# Revit family: S90.196.xxx(.WDAS)_with 3 shelves_4+6 drawers
name_source: partatom
category: Möbelsysteme
revit_build: Autodesk Revit 2015 (Build: 20160512_1515(x64)
units: mm (PartAtom-declared; Revit-internal decimal feet)

## types (27) — shared parameters
Air duct distance = 130 mm  [stored 0.426509 ft]
Beschreibung = GS-tested safety storage cabinets for unrestricted storage of flammable hazardous materials in work areas in accordance with EN 14470-1 and TRGS 510 with a fire resistance of 90 (Type 90)
Cabinet depth = 617 mm
Cabinet height = 1968 mm  [stored 6.45669 ft]
Diff. pressure (Air change 10 times) = 5.0 Pa
Hersteller = asecos GmbH
Price information = Price from fall 2017
Price information 2 = Prices are ex works and without taxes and shipping
Product video = https://www.youtube.com
URL = https://www.asecos.com

## per-type parameters (varying)
- S90.196.060 with 3 shelves, warning yellow: 1200 mm 3 shelves=Nein; 1200 mm 4 drawers=Nein; 1200 mm 6 drawers=Nein; 600 mm 3 shelves=Ja; 600 mm 4 drawers=Nein; 600 mm 6 drawers=Nein; 900 mm 3 shelves=Nein; 900 mm 4 drawers=Nein; 900 mm 6 drawers=Nein; Air change 10 times=1.1 L/s; Bestellnummer DACH=30228-002-30249; Cabinet & door colour=RAL 1004 warning yellow; Cabinet width=597 mm; Distributed load=8.77 kN/m²; Door width=514 mm  [stored 1.68635 ft]; Double door=Nein; Handle position=514 mm  [stored 1.68635 ft]; Kosten=2093 $; Modell=S90.196.060.WDAS with 3 shelves and door open arrest system; Order No. Global=30228-002-33659; Single door=Ja; Sticker position lb=269 mm; Sticker position ls=555 mm; Sticker position rb=0 mm  [stored 0 ft]; Typenbild=30227-002.jpg; ex. air 2 depth=5 mm  [stored 0.0164042 ft]; ex. air pos. 1=368 mm  [stored 1.20735 ft]; ex.air 1 depth=-5 mm  [stored -0.0164042 ft]
- S90.196.060 with 3 shelves, light grey: 1200 mm 3 shelves=Nein; 1200 mm 4 drawers=Nein; 1200 mm 6 drawers=Nein; 600 mm 3 shelves=Ja; 600 mm 4 drawers=Nein; 600 mm 6 drawers=Nein; 900 mm 3 shelves=Nein; 900 mm 4 drawers=Nein; 900 mm 6 drawers=Nein; Air change 10 times=1.1 L/s; Bestellnummer DACH=30228-001-30249; Cabinet & door colour=RAL 7035 Light grey; Cabinet width=597 mm; Distributed load=8.77 kN/m²; Door width=514 mm  [stored 1.68635 ft]; Double door=Nein; Handle position=514 mm  [stored 1.68635 ft]; Kosten=2093 $; Modell=S90.196.060.WDAS with 3 shelves and door open arrest system; Order No. Global=30228-001-33659; Single door=Ja; Sticker position lb=269 mm; Sticker position ls=555 mm; Sticker position rb=0 mm  [stored 0 ft]; Typenbild=30227-001.jpg; ex. air 2 depth=5 mm  [stored 0.0164042 ft]; ex. air pos. 1=368 mm  [stored 1.20735 ft]; ex.air 1 depth=-5 mm  [stored -0.0164042 ft]
- S90.196.060 with 3 shelves, pure white: 1200 mm 3 shelves=Nein; 1200 mm 4 drawers=Nein; 1200 mm 6 drawers=Nein; 600 mm 3 shelves=Ja; 600 mm 4 drawers=Nein; 600 mm 6 drawers=Nein; 900 mm 3 shelves=Nein; 900 mm 4 drawers=Nein; 900 mm 6 drawers=Nein; Air change 10 times=1.1 L/s; Bestellnummer DACH=30228-005-30249; Cabinet & door colour=RAL 9010 Pure white; Cabinet width=597 mm; Distributed load=8.77 kN/m²; Door width=514 mm  [stored 1.68635 ft]; Double door=Nein; Handle position=514 mm  [stored 1.68635 ft]; Kosten=2093 $; Modell=S90.196.060.WDAS with 3 shelves and door open arrest system; Order No. Global=30228-005-33659; Single door=Ja; Sticker position lb=269 mm; Sticker position ls=555 mm; Sticker position rb=0 mm  [stored 0 ft]; Typenbild=30227-001.jpg; ex. air 2 depth=5 mm  [stored 0.0164042 ft]; ex. air pos. 1=368 mm  [stored 1.20735 ft]; ex.air 1 depth=-5 mm  [stored -0.0164042 ft]
- S90.196.060 with 4 drawers, warning yellow: 1200 mm 3 shelves=Nein; 1200 mm 4 drawers=Nein; 1200 mm 6 drawers=Nein; 600 mm 3 shelves=Nein; 600 mm 4 drawers=Ja; 600 mm 6 drawers=Nein; 900 mm 3 shelves=Nein; 900 mm 4 drawers=Nein; 900 mm 6 drawers=Nein; Air change 10 times=1.1 L/s; Bestellnummer DACH=30228-002-30267; Cabinet & door colour=RAL 1004 warning yellow; Cabinet width=597 mm; Distributed load=8.77 kN/m²; Door width=514 mm  [stored 1.68635 ft]; Double door=Nein; Handle position=514 mm  [stored 1.68635 ft]; Kosten=2373 $; Modell=S90.196.060.WDAS with 4 drawers and door open arrest system; Order No. Global=30228-002-33681; Single door=Ja; Sticker position lb=269 mm; Sticker position ls=555 mm; Sticker position rb=0 mm  [stored 0 ft]; Typenbild=30227-002.jpg; ex. air 2 depth=5 mm  [stored 0.0164042 ft]; ex. air pos. 1=368 mm  [stored 1.20735 ft]; ex.air 1 depth=-5 mm  [stored -0.0164042 ft]
- S90.196.060 with 4 drawers, light grey: 1200 mm 3 shelves=Nein; 1200 mm 4 drawers=Nein; 1200 mm 6 drawers=Nein; 600 mm 3 shelves=Nein; 600 mm 4 drawers=Ja; 600 mm 6 drawers=Nein; 900 mm 3 shelves=Nein; 900 mm 4 drawers=Nein; 900 mm 6 drawers=Nein; Air change 10 times=1.1 L/s; Bestellnummer DACH=30228-001-30267; Cabinet & door colour=RAL 7035 Light grey; Cabinet width=597 mm; Distributed load=8.77 kN/m²; Door width=514 mm  [stored 1.68635 ft]; Double door=Nein; Handle position=514 mm  [stored 1.68635 ft]; Kosten=2373 $; Modell=S90.196.060.WDAS with 4 drawer and door open arrest systems; Order No. Global=30228-001-33681; Single door=Ja; Sticker position lb=269 mm; Sticker position ls=555 mm; Sticker position rb=0 mm  [stored 0 ft]; Typenbild=30227-001.jpg; ex. air 2 depth=5 mm  [stored 0.0164042 ft]; ex. air pos. 1=368 mm  [stored 1.20735 ft]; ex.air 1 depth=-5 mm  [stored -0.0164042 ft]
- S90.196.060 with 4 drawers, pure white: 1200 mm 3 shelves=Nein; 1200 mm 4 drawers=Nein; 1200 mm 6 drawers=Nein; 600 mm 3 shelves=Nein; 600 mm 4 drawers=Ja; 600 mm 6 drawers=Nein; 900 mm 3 shelves=Nein; 900 mm 4 drawers=Nein; 900 mm 6 drawers=Nein; Air change 10 times=1.1 L/s; Bestellnummer DACH=30228-005-30267; Cabinet & door colour=RAL 9010 Pure white; Cabinet width=597 mm; Distributed load=8.77 kN/m²; Door width=514 mm  [stored 1.68635 ft]; Double door=Nein; Handle position=514 mm  [stored 1.68635 ft]; Kosten=2373 $; Modell=S90.196.060.WDAS with 4 drawers and door open arrest system; Order No. Global=30228-005-33681; Single door=Ja; Sticker position lb=269 mm; Sticker position ls=555 mm; Sticker position rb=0 mm  [stored 0 ft]; Typenbild=30227-001.jpg; ex. air 2 depth=5 mm  [stored 0.0164042 ft]; ex. air pos. 1=368 mm  [stored 1.20735 ft]; ex.air 1 depth=-5 mm  [stored -0.0164042 ft]
- S90.196.060 with 6 drawers, warning yellow: 1200 mm 3 shelves=Nein; 1200 mm 4 drawers=Nein; 1200 mm 6 drawers=Nein; 600 mm 3 shelves=Nein; 600 mm 4 drawers=Nein; 600 mm 6 drawers=Ja; 900 mm 3 shelves=Nein; 900 mm 4 drawers=Nein; 900 mm 6 drawers=Nein; Air change 10 times=1.1 L/s; Bestellnummer DACH=30228-002-30269; Cabinet & door colour=RAL 1004 warning yellow; Cabinet width=597 mm; Distributed load=8.77 kN/m²; Door width=514 mm  [stored 1.68635 ft]; Double door=Nein; Handle position=514 mm  [stored 1.68635 ft]; Kosten=2595 $; Modell=S90.196.060.WDAS with 6 drawers and door open arrest system; Order No. Global=30228-002-33683; Single door=Ja; Sticker position lb=269 mm; Sticker position ls=555 mm; Sticker position rb=0 mm  [stored 0 ft]; Typenbild=30227-002.jpg; ex. air 2 depth=5 mm  [stored 0.0164042 ft]; ex. air pos. 1=368 mm  [stored 1.20735 ft]; ex.air 1 depth=-5 mm  [stored -0.0164042 ft]
- S90.196.060 with 6 drawers, light grey: 1200 mm 3 shelves=Nein; 1200 mm 4 drawers=Nein; 1200 mm 6 drawers=Nein; 600 mm 3 shelves=Nein; 600 mm 4 drawers=Nein; 600 mm 6 drawers=Ja; 900 mm 3 shelves=Nein; 900 mm 4 drawers=Nein; 900 mm 6 drawers=Nein; Air change 10 times=1.1 L/s; Bestellnummer DACH=30228-001-30269; Cabinet & door colour=RAL 7035 Light grey; Cabinet width=597 mm; Distributed load=8.77 kN/m²; Door width=514 mm  [stored 1.68635 ft]; Double door=Nein; Handle position=514 mm  [stored 1.68635 ft]; Kosten=2595 $; Modell=S90.196.060.WDAS with 6 drawers and door open arrest system; Order No. Global=30228-001-33683; Single door=Ja; Sticker position lb=269 mm; Sticker position ls=555 mm; Sticker position rb=0 mm  [stored 0 ft]; Typenbild=30227-001.jpg; ex. air 2 depth=5 mm  [stored 0.0164042 ft]; ex. air pos. 1=368 mm  [stored 1.20735 ft]; ex.air 1 depth=-5 mm  [stored -0.0164042 ft]
- S90.196.060 with 6 drawers, pure white: 1200 mm 3 shelves=Nein; 1200 mm 4 drawers=Nein; 1200 mm 6 drawers=Nein; 600 mm 3 shelves=Nein; 600 mm 4 drawers=Nein; 600 mm 6 drawers=Ja; 900 mm 3 shelves=Nein; 900 mm 4 drawers=Nein; 900 mm 6 drawers=Nein; Air change 10 times=1.1 L/s; Bestellnummer DACH=30228-005-30269; Cabinet & door colour=RAL 9010 Pure white; Cabinet width=597 mm; Distributed load=8.77 kN/m²; Door width=514 mm  [stored 1.68635 ft]; Double door=Nein; Handle position=514 mm  [stored 1.68635 ft]; Kosten=2595 $; Modell=S90.196.060.WDAS with 6 drawers and door open arrest system; Order No. Global=30228-005-33683; Single door=Ja; Sticker position lb=269 mm; Sticker position ls=555 mm; Sticker position rb=0 mm  [stored 0 ft]; Typenbild=30227-001.jpg; ex. air 2 depth=5 mm  [stored 0.0164042 ft]; ex. air pos. 1=368 mm  [stored 1.20735 ft]; ex.air 1 depth=-5 mm  [stored -0.0164042 ft]
- S90.196.090 with 3 shelves, warning yellow: 1200 mm 3 shelves=Nein; 1200 mm 4 drawers=Nein; 1200 mm 6 drawers=Nein; 600 mm 3 shelves=Nein; 600 mm 4 drawers=Nein; 600 mm 6 drawers=Nein; 900 mm 3 shelves=Ja; 900 mm 4 drawers=Nein; 900 mm 6 drawers=Nein; Air change 10 times=1.7 L/s; Bestellnummer DACH=30205-002-30208; Cabinet & door colour=RAL 1004 warning yellow; Cabinet width=897 mm; Distributed load=6.41 kN/m²; Door width=403 mm; Double door=Ja; Handle position=401 mm; Kosten=2599.5 $; Modell=S90.196.090.WDAS with 3 shelves and door open arrest system; Order No. Global=30205-002-33705; Single door=Nein; Sticker position lb=156 mm; Sticker position ls=663 mm; Sticker position rb=220 mm  [stored 0.721785 ft]; Typenbild=30204-002.jpg; ex. air 2 depth=-5 mm  [stored -0.0164042 ft]; ex. air pos. 1=503 mm  [stored 1.65026 ft]; ex.air 1 depth=5 mm  [stored 0.0164042 ft]
- S90.196.090 with 3 shelves, light grey: 1200 mm 3 shelves=Nein; 1200 mm 4 drawers=Nein; 1200 mm 6 drawers=Nein; 600 mm 3 shelves=Nein; 600 mm 4 drawers=Nein; 600 mm 6 drawers=Nein; 900 mm 3 shelves=Ja; 900 mm 4 drawers=Nein; 900 mm 6 drawers=Nein; Air change 10 times=1.7 L/s; Bestellnummer DACH=30205-001-30208; Cabinet & door colour=RAL 7035 Light grey; Cabinet width=897 mm; Distributed load=6.41 kN/m²; Door width=403 mm; Double door=Ja; Handle position=401 mm; Kosten=2599.5 $; Modell=S90.196.090.WDAS with 3 shelves and door open arrest system; Order No. Global=30205-001-33705; Single door=Nein; Sticker position lb=156 mm; Sticker position ls=663 mm; Sticker position rb=220 mm  [stored 0.721785 ft]; Typenbild=30204-001.jpg; ex. air 2 depth=-5 mm  [stored -0.0164042 ft]; ex. air pos. 1=503 mm  [stored 1.65026 ft]; ex.air 1 depth=5 mm  [stored 0.0164042 ft]
- S90.196.090 with 3 shelves, pure white: 1200 mm 3 shelves=Nein; 1200 mm 4 drawers=Nein; 1200 mm 6 drawers=Nein; 600 mm 3 shelves=Nein; 600 mm 4 drawers=Nein; 600 mm 6 drawers=Nein; 900 mm 3 shelves=Ja; 900 mm 4 drawers=Nein; 900 mm 6 drawers=Nein; Air change 10 times=1.7 L/s; Bestellnummer DACH=30205-005-30208; Cabinet & door colour=RAL 9010 Pure white; Cabinet width=897 mm; Distributed load=6.41 kN/m²; Door width=403 mm; Double door=Ja; Handle position=401 mm; Kosten=2599.5 $; Modell=S90.196.090.WDAS with 3 shelves and door open arrest system; Order No. Global=30205-005-33705; Single door=Nein; Sticker position lb=156 mm; Sticker position ls=663 mm; Sticker position rb=220 mm  [stored 0.721785 ft]; Typenbild=30204-001.jpg; ex. air 2 depth=-5 mm  [stored -0.0164042 ft]; ex. air pos. 1=503 mm  [stored 1.65026 ft]; ex.air 1 depth=5 mm  [stored 0.0164042 ft]
- S90.196.090 with 4 drawers, warning yellow: 1200 mm 3 shelves=Nein; 1200 mm 4 drawers=Nein; 1200 mm 6 drawers=Nein; 600 mm 3 shelves=Nein; 600 mm 4 drawers=Nein; 600 mm 6 drawers=Nein; 900 mm 3 shelves=Nein; 900 mm 4 drawers=Ja; 900 mm 6 drawers=Nein; Air change 10 times=1.7 L/s; Bestellnummer DACH=30205-002-30218; Cabinet & door colour=RAL 1004 warning yellow; Cabinet width=897 mm; Distributed load=6.41 kN/m²; Door width=403 mm; Double door=Ja; Handle position=401 mm; Kosten=3106 $; Modell=S90.196.090.WDAS with 4 drawers and door open arrest system; Order No. Global=30205-002-33709; Single door=Nein; Sticker position lb=156 mm; Sticker position ls=663 mm; Sticker position rb=220 mm  [stored 0.721785 ft]; Typenbild=30204-002.jpg; ex. air 2 depth=-5 mm  [stored -0.0164042 ft]; ex. air pos. 1=503 mm  [stored 1.65026 ft]; ex.air 1 depth=5 mm  [stored 0.0164042 ft]
- S90.196.090 with 4 drawers, light grey: 1200 mm 3 shelves=Nein; 1200 mm 4 drawers=Nein; 1200 mm 6 drawers=Nein; 600 mm 3 shelves=Nein; 600 mm 4 drawers=Nein; 600 mm 6 drawers=Nein; 900 mm 3 shelves=Nein; 900 mm 4 drawers=Ja; 900 mm 6 drawers=Nein; Air change 10 times=1.7 L/s; Bestellnummer DACH=30205-001-30218; Cabinet & door colour=RAL 7035 Light grey; Cabinet width=897 mm; Distributed load=6.41 kN/m²; Door width=403 mm; Double door=Ja; Handle position=401 mm; Kosten=3106 $; Modell=S90.196.090.WDAS with 4 drawers and door open arrest system; Order No. Global=30205-001-33709; Single door=Nein; Sticker position lb=156 mm; Sticker position ls=663 mm; Sticker position rb=220 mm  [stored 0.721785 ft]; Typenbild=30204-001.jpg; ex. air 2 depth=-5 mm  [stored -0.0164042 ft]; ex. air pos. 1=503 mm  [stored 1.65026 ft]; ex.air 1 depth=5 mm  [stored 0.0164042 ft]
- S90.196.090 with 4 drawers, pure white: 1200 mm 3 shelves=Nein; 1200 mm 4 drawers=Nein; 1200 mm 6 drawers=Nein; 600 mm 3 shelves=Nein; 600 mm 4 drawers=Nein; 600 mm 6 drawers=Nein; 900 mm 3 shelves=Nein; 900 mm 4 drawers=Ja; 900 mm 6 drawers=Nein; Air change 10 times=1.7 L/s; Bestellnummer DACH=30205-005-30218; Cabinet & door colour=RAL 9010 Pure white; Cabinet width=897 mm; Distributed load=6.41 kN/m²; Door width=403 mm; Double door=Ja; Handle position=401 mm; Kosten=3106 $; Modell=S90.196.090.WDAS with 4 drawers and door open arrest system; Order No. Global=30205-005-33709; Single door=Nein; Sticker position lb=156 mm; Sticker position ls=663 mm; Sticker position rb=220 mm  [stored 0.721785 ft]; Typenbild=30204-001.jpg; ex. air 2 depth=-5 mm  [stored -0.0164042 ft]; ex. air pos. 1=503 mm  [stored 1.65026 ft]; ex.air 1 depth=5 mm  [stored 0.0164042 ft]
- S90.196.090 with 6 drawers, warning yellow: 1200 mm 3 shelves=Nein; 1200 mm 4 drawers=Nein; 1200 mm 6 drawers=Nein; 600 mm 3 shelves=Nein; 600 mm 4 drawers=Nein; 600 mm 6 drawers=Nein; 900 mm 3 shelves=Nein; 900 mm 4 drawers=Nein; 900 mm 6 drawers=Ja; Air change 10 times=1.7 L/s; Bestellnummer DACH=30205-002-30220; Cabinet & door colour=RAL 1004 warning yellow; Cabinet width=897 mm; Distributed load=6.41 kN/m²; Door width=403 mm; Double door=Ja; Handle position=401 mm; Kosten=3456 $; Modell=S90.196.090.WDAS with 6 drawers and door open arrest system; Order No. Global=30205-002-33711; Single door=Nein; Sticker position lb=156 mm; Sticker position ls=663 mm; Sticker position rb=220 mm  [stored 0.721785 ft]; Typenbild=30204-002.jpg; ex. air 2 depth=-5 mm  [stored -0.0164042 ft]; ex. air pos. 1=503 mm  [stored 1.65026 ft]; ex.air 1 depth=5 mm  [stored 0.0164042 ft]
- S90.196.090 with 6 drawers, light grey: 1200 mm 3 shelves=Nein; 1200 mm 4 drawers=Nein; 1200 mm 6 drawers=Nein; 600 mm 3 shelves=Nein; 600 mm 4 drawers=Nein; 600 mm 6 drawers=Nein; 900 mm 3 shelves=Nein; 900 mm 4 drawers=Nein; 900 mm 6 drawers=Ja; Air change 10 times=1.7 L/s; Bestellnummer DACH=30205-001-30220; Cabinet & door colour=RAL 7035 Light grey; Cabinet width=897 mm; Distributed load=6.41 kN/m²; Door width=403 mm; Double door=Ja; Handle position=401 mm; Kosten=3456 $; Modell=S90.196.090.WDAS with 6 drawers and door open arrest system; Order No. Global=30205-001-33711; Single door=Nein; Sticker position lb=156 mm; Sticker position ls=663 mm; Sticker position rb=220 mm  [stored 0.721785 ft]; Typenbild=30204-001.jpg; ex. air 2 depth=-5 mm  [stored -0.0164042 ft]; ex. air pos. 1=503 mm  [stored 1.65026 ft]; ex.air 1 depth=5 mm  [stored 0.0164042 ft]
- S90.196.090 with 6 drawers, pure white: 1200 mm 3 shelves=Nein; 1200 mm 4 drawers=Nein; 1200 mm 6 drawers=Nein; 600 mm 3 shelves=Nein; 600 mm 4 drawers=Nein; 600 mm 6 drawers=Nein; 900 mm 3 shelves=Nein; 900 mm 4 drawers=Nein; 900 mm 6 drawers=Ja; Air change 10 times=1.7 L/s; Bestellnummer DACH=30205-005-30220; Cabinet & door colour=RAL 9010 Pure white; Cabinet width=897 mm; Distributed load=6.41 kN/m²; Door width=403 mm; Double door=Ja; Handle position=401 mm; Kosten=3456 $; Modell=S90.196.090.WDAS with 6 drawers and door open arrest system; Order No. Global=30205-005-33711; Single door=Nein; Sticker position lb=156 mm; Sticker position ls=663 mm; Sticker position rb=220 mm  [stored 0.721785 ft]; Typenbild=30204-001.jpg; ex. air 2 depth=-5 mm  [stored -0.0164042 ft]; ex. air pos. 1=503 mm  [stored 1.65026 ft]; ex.air 1 depth=5 mm  [stored 0.0164042 ft]
- S90.196.120 with 3 shelves, warning yellow: 1200 mm 3 shelves=Ja; 1200 mm 4 drawers=Nein; 1200 mm 6 drawers=Nein; 600 mm 3 shelves=Nein; 600 mm 4 drawers=Nein; 600 mm 6 drawers=Nein; 900 mm 3 shelves=Nein; 900 mm 4 drawers=Nein; 900 mm 6 drawers=Nein; Air change 10 times=2.5 L/s; Bestellnummer DACH=30116-002-30127; Cabinet & door colour=RAL 1004 warning yellow; Cabinet width=1197 mm; Distributed load=4.16 kN/m²; Door width=553 mm; Double door=Ja; Handle position=551 mm; Kosten=2701.5 $; Modell=S90.196.120.WDAS with 3 shelves and door open arrest system; Order No. Global=30116-002-33715; Single door=Nein; Sticker position lb=156 mm; Sticker position ls=813 mm; Sticker position rb=220 mm  [stored 0.721785 ft]; Typenbild=30115-002.jpg; ex. air 2 depth=-5 mm  [stored -0.0164042 ft]; ex. air pos. 1=653 mm  [stored 2.14239 ft]; ex.air 1 depth=5 mm  [stored 0.0164042 ft]
- S90.196.120 with 3 shelves, light grey: 1200 mm 3 shelves=Ja; 1200 mm 4 drawers=Nein; 1200 mm 6 drawers=Nein; 600 mm 3 shelves=Nein; 600 mm 4 drawers=Nein; 600 mm 6 drawers=Nein; 900 mm 3 shelves=Nein; 900 mm 4 drawers=Nein; 900 mm 6 drawers=Nein; Air change 10 times=2.5 L/s; Bestellnummer DACH=30116-001-30127; Cabinet & door colour=RAL 7035 Light grey; Cabinet width=1197 mm; Distributed load=4.16 kN/m²; Door width=553 mm; Double door=Ja; Handle position=551 mm; Kosten=2701.5 $; Modell=S90.196.120.WDAS with 3 shelves and door open arrest system; Order No. Global=30116-001-33715; Single door=Nein; Sticker position lb=156 mm; Sticker position ls=813 mm; Sticker position rb=220 mm  [stored 0.721785 ft]; Typenbild=30115-001.jpg; ex. air 2 depth=-5 mm  [stored -0.0164042 ft]; ex. air pos. 1=653 mm  [stored 2.14239 ft]; ex.air 1 depth=5 mm  [stored 0.0164042 ft]
- S90.196.120 with 3 shelves, pure white: 1200 mm 3 shelves=Ja; 1200 mm 4 drawers=Nein; 1200 mm 6 drawers=Nein; 600 mm 3 shelves=Nein; 600 mm 4 drawers=Nein; 600 mm 6 drawers=Nein; 900 mm 3 shelves=Nein; 900 mm 4 drawers=Nein; 900 mm 6 drawers=Nein; Air change 10 times=2.5 L/s; Bestellnummer DACH=30116-005-30127; Cabinet & door colour=RAL 9010 Pure white; Cabinet width=1197 mm; Distributed load=4.16 kN/m²; Door width=553 mm; Double door=Ja; Handle position=551 mm; Kosten=2701.5 $; Modell=S90.196.120.WDAS with 3 shelves and door open arrest system; Order No. Global=30116-005-33715; Single door=Nein; Sticker position lb=156 mm; Sticker position ls=813 mm; Sticker position rb=220 mm  [stored 0.721785 ft]; Typenbild=30115-001.jpg; ex. air 2 depth=-5 mm  [stored -0.0164042 ft]; ex. air pos. 1=653 mm  [stored 2.14239 ft]; ex.air 1 depth=5 mm  [stored 0.0164042 ft]
- S90.196.120 with 4 drawers, warning yellow: 1200 mm 3 shelves=Nein; 1200 mm 4 drawers=Ja; 1200 mm 6 drawers=Nein; 600 mm 3 shelves=Nein; 600 mm 4 drawers=Nein; 600 mm 6 drawers=Nein; 900 mm 3 shelves=Nein; 900 mm 4 drawers=Nein; 900 mm 6 drawers=Nein; Air change 10 times=2.5 L/s; Bestellnummer DACH=30116-002-30147; Cabinet & door colour=RAL 1004 warning yellow; Cabinet width=1197 mm; Distributed load=4.16 kN/m²; Door width=553 mm; Double door=Ja; Handle position=551 mm; Kosten=3208 $; Modell=S90.196.120.WDAS with 4 drawers and door open arrest system; Order No. Global=30116-002-33724; Single door=Nein; Sticker position lb=156 mm; Sticker position ls=813 mm; Sticker position rb=220 mm  [stored 0.721785 ft]; Typenbild=30115-002.jpg; ex. air 2 depth=-5 mm  [stored -0.0164042 ft]; ex. air pos. 1=653 mm  [stored 2.14239 ft]; ex.air 1 depth=5 mm  [stored 0.0164042 ft]
- S90.196.120 with 4 drawers, light grey: 1200 mm 3 shelves=Nein; 1200 mm 4 drawers=Ja; 1200 mm 6 drawers=Nein; 600 mm 3 shelves=Nein; 600 mm 4 drawers=Nein; 600 mm 6 drawers=Nein; 900 mm 3 shelves=Nein; 900 mm 4 drawers=Nein; 900 mm 6 drawers=Nein; Air change 10 times=2.5 L/s; Bestellnummer DACH=30116-001-30147; Cabinet & door colour=RAL 7035 Light grey; Cabinet width=1197 mm; Distributed load=4.16 kN/m²; Door width=553 mm; Double door=Ja; Handle position=551 mm; Kosten=3208 $; Modell=S90.196.120.WDAS with 4 drawers and door open arrest system; Order No. Global=30116-001-33724; Single door=Nein; Sticker position lb=156 mm; Sticker position ls=813 mm; Sticker position rb=220 mm  [stored 0.721785 ft]; Typenbild=30115-001.jpg; ex. air 2 depth=-5 mm  [stored -0.0164042 ft]; ex. air pos. 1=653 mm  [stored 2.14239 ft]; ex.air 1 depth=5 mm  [stored 0.0164042 ft]
- S90.196.120 with 4 drawers, pure white: 1200 mm 3 shelves=Nein; 1200 mm 4 drawers=Ja; 1200 mm 6 drawers=Nein; 600 mm 3 shelves=Nein; 600 mm 4 drawers=Nein; 600 mm 6 drawers=Nein; 900 mm 3 shelves=Nein; 900 mm 4 drawers=Nein; 900 mm 6 drawers=Nein; Air change 10 times=2.5 L/s; Bestellnummer DACH=30116-005-30147; Cabinet & door colour=RAL 9010 Pure white; Cabinet width=1197 mm; Distributed load=4.16 kN/m²; Door width=553 mm; Double door=Ja; Handle position=551 mm; Kosten=3208 $; Modell=S90.196.120.WDAS with 4 drawers and door open arrest system; Order No. Global=30116-005-33724; Single door=Nein; Sticker position lb=156 mm; Sticker position ls=813 mm; Sticker position rb=220 mm  [stored 0.721785 ft]; Typenbild=30115-001.jpg; ex. air 2 depth=-5 mm  [stored -0.0164042 ft]; ex. air pos. 1=653 mm  [stored 2.14239 ft]; ex.air 1 depth=5 mm  [stored 0.0164042 ft]
- S90.196.120 with 6 drawers, warning yellow: 1200 mm 3 shelves=Nein; 1200 mm 4 drawers=Nein; 1200 mm 6 drawers=Ja; 600 mm 3 shelves=Nein; 600 mm 4 drawers=Nein; 600 mm 6 drawers=Nein; 900 mm 3 shelves=Nein; 900 mm 4 drawers=Nein; 900 mm 6 drawers=Nein; Air change 10 times=2.5 L/s; Bestellnummer DACH=30116-002-30149; Cabinet & door colour=RAL 1004 warning yellow; Cabinet width=1197 mm; Distributed load=4.16 kN/m²; Door width=553 mm; Double door=Ja; Handle position=551 mm; Kosten=3558 $; Modell=S90.196.120.WDAS with 6 drawers and door open arrest system; Order No. Global=30116-002-33726; Single door=Nein; Sticker position lb=156 mm; Sticker position ls=813 mm; Sticker position rb=220 mm  [stored 0.721785 ft]; Typenbild=30115-002.jpg; ex. air 2 depth=-5 mm  [stored -0.0164042 ft]; ex. air pos. 1=653 mm  [stored 2.14239 ft]; ex.air 1 depth=5 mm  [stored 0.0164042 ft]
- S90.196.120 with 6 drawers, light grey: 1200 mm 3 shelves=Nein; 1200 mm 4 drawers=Nein; 1200 mm 6 drawers=Ja; 600 mm 3 shelves=Nein; 600 mm 4 drawers=Nein; 600 mm 6 drawers=Nein; 900 mm 3 shelves=Nein; 900 mm 4 drawers=Nein; 900 mm 6 drawers=Nein; Air change 10 times=2.5 L/s; Bestellnummer DACH=30116-001-30149; Cabinet & door colour=RAL 7035 Light grey; Cabinet width=1197 mm; Distributed load=4.16 kN/m²; Door width=553 mm; Double door=Ja; Handle position=551 mm; Kosten=3558 $; Modell=S90.196.120.WDAS with 6 drawers and door open arrest system; Order No. Global=30116-001-33726; Single door=Nein; Sticker position lb=156 mm; Sticker position ls=813 mm; Sticker position rb=220 mm  [stored 0.721785 ft]; Typenbild=30115-001.jpg; ex. air 2 depth=-5 mm  [stored -0.0164042 ft]; ex. air pos. 1=653 mm  [stored 2.14239 ft]; ex.air 1 depth=5 mm  [stored 0.0164042 ft]
- S90.196.120 with 6 drawers, pure white: 1200 mm 3 shelves=Nein; 1200 mm 4 drawers=Nein; 1200 mm 6 drawers=Ja; 600 mm 3 shelves=Nein; 600 mm 4 drawers=Nein; 600 mm 6 drawers=Nein; 900 mm 3 shelves=Nein; 900 mm 4 drawers=Nein; 900 mm 6 drawers=Nein; Air change 10 times=2.5 L/s; Bestellnummer DACH=30116-005-30149; Cabinet & door colour=RAL 9010 Pure white; Cabinet width=1197 mm; Distributed load=4.16 kN/m²; Door width=553 mm; Double door=Ja; Handle position=551 mm; Kosten=3558 $; Modell=S90.196.120.WDAS with 6 drawers and door open arrest system; Order No. Global=30116-005-33726; Single door=Nein; Sticker position lb=156 mm; Sticker position ls=813 mm; Sticker position rb=220 mm  [stored 0.721785 ft]; Typenbild=30115-001.jpg; ex. air 2 depth=-5 mm  [stored -0.0164042 ft]; ex. air pos. 1=653 mm  [stored 2.14239 ft]; ex.air 1 depth=5 mm  [stored 0.0164042 ft]

note: [stored X ft] marks values corroborated as IEEE doubles in the binary element streams (Revit-internal decimal feet)
